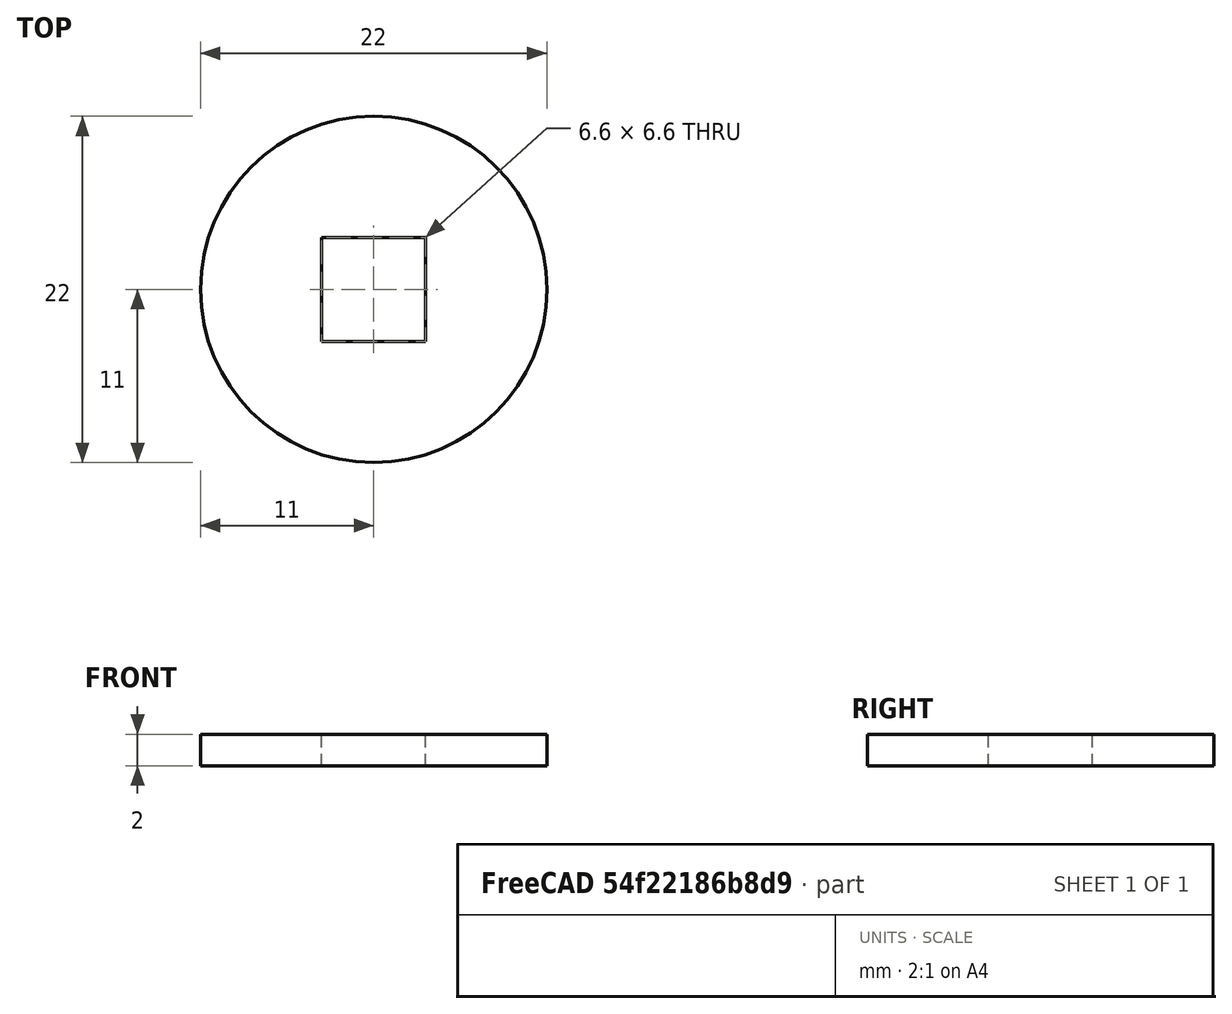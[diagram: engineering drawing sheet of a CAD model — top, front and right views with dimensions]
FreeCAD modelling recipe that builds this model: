
FCSTD DOCUMENT  (FreeCAD 0.15R4671 (Git))
Label: DIN440_CLASS_V_M6
License: CreativeCommons Attribution-ShareAlike
LicenseURL: http://creativecommons.org/licenses/by-sa/4.0/
objects: Sketcher::SketchObject×1, PartDesign::Pad×1
note: 3 computed .brp shape members not serialized (recipe doc carries the construction recipe); baked Part::Feature solids carry a one-line shape summary decoded from their .brp

FEATURE [Sketcher::SketchObject] Sketch
  sketch-geometry (5):
    g0: Circle CenterX=0 CenterY=0 CenterZ=0 NormalX=0 NormalY=0 NormalZ=1 Radius=11
    g1: LineSegment StartX=-3.3 StartY=3.3 StartZ=0 EndX=3.3 EndY=3.3 EndZ=0
    g2: LineSegment StartX=3.3 StartY=3.3 StartZ=0 EndX=3.3 EndY=-3.3 EndZ=0
    g3: LineSegment StartX=3.3 StartY=-3.3 StartZ=0 EndX=-3.3 EndY=-3.3 EndZ=0
    g4: LineSegment StartX=-3.3 StartY=-3.3 StartZ=0 EndX=-3.3 EndY=3.3 EndZ=0
  constraints (15):
    c: Coincident(g0,g-1)
    c: Radius(g0) = 11
    c: Coincident(g1,g2)
    c: Coincident(g2,g3)
    c: Coincident(g3,g4)
    c: Coincident(g4,g1)
    c: Horizontal(g1)
    c: Horizontal(g3)
    c: Vertical(g2)
    c: Vertical(g4)
    c: Equal(g1,g4)
    c: Equal(g4,g3)
    c: Equal(g3,g2)
    c: DistanceX(g1,g1) = 6.6
    c: Symmetric(g2,g1,g-1)
FEATURE [PartDesign::Pad] Pad
  Length = 2
  Length2 = 100
  Sketch = -> Sketch
  Type = 0
